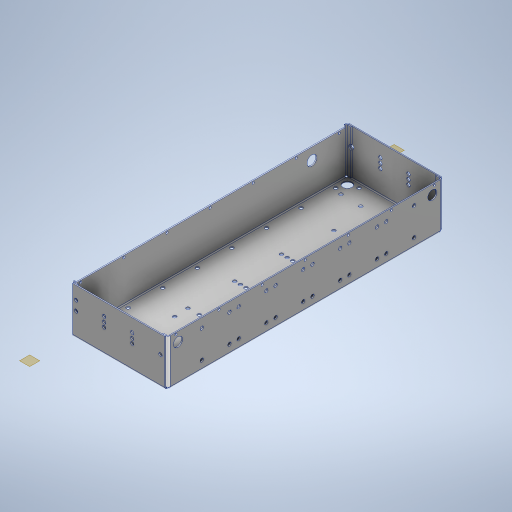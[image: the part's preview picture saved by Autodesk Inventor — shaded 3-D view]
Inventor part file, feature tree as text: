
AUTODESK INVENTOR PART (.ipt)
format: ipt  version: 2023 (Build 270158000, 158)  size: 754,176 bytes
history: native  units: in
note: dims shown in document units (in); Inventor stores cm internally (conversion verified against a paired STEP export)
features: sketch x25, hole x20, sheet_metal_op x12, pattern_linear x12, other x7, plane x4
ambient origin geometry x8: Origin, YZ Plane, XZ Plane, XY Plane, X Axis, Y Axis, Z Axis, Center Point
bodies: Solid1 (feature_tree)
feature tree (80):
  sheet_metal_op  "Face1"
  sheet_metal_op  "Flange1"
  sheet_metal_op  "Flange2"
  sheet_metal_op  "Unfold1"
  hole  "Hole1"  [1 undecoded]
  pattern_linear  "Rectangular Pattern1"  Count1=30  [1 undecoded]
  pattern_linear  "Rectangular Pattern2"  Count1=10  [1 undecoded]
  hole  "Hole2"  [1 undecoded]
  pattern_linear  "Rectangular Pattern3"  Count1=10 Spacing1=90.0deg
  hole  "Hole3"  [1 undecoded]
  hole  "Hole6"  [1 undecoded]
  pattern_linear  "Rectangular Pattern6"  Count1=10 Spacing1=90.0deg
  plane  "Work Plane4"
  hole  "Hole7"  [1 undecoded]
  plane  "Work Plane3"
  hole  "Hole8"  [1 undecoded]
  plane  "Work Plane2"
  hole  "Hole9"  [1 undecoded]
  plane  "Work Plane1"
  hole  "Hole10"  [1 undecoded]
  hole  "Hole11"  [1 undecoded]
  hole  "Hole12"  [1 undecoded]
  hole  "Hole13"  [1 undecoded]
  pattern_linear  "Rectangular Pattern11"  Count1=6  [1 undecoded]
  pattern_linear  "Rectangular Pattern12"  Count1=6  [1 undecoded]
  pattern_linear  "Rectangular Pattern13"  Count1=6  [1 undecoded]
  pattern_linear  "Rectangular Pattern14"  Count1=2  [1 undecoded]
  sheet_metal_op  "Refold6"
  sheet_metal_op  "Flange8"
  hole  "Hole14"  [1 undecoded]
  hole  "Hole15"  [1 undecoded]
  hole  "Hole16"  [1 undecoded]
  hole  "Hole17"  [1 undecoded]
  hole  "Hole18"  [1 undecoded]
  hole  "Hole19"  [1 undecoded]
  pattern_linear  "Rectangular Pattern15"  Count1=3  [1 undecoded]
  hole  "Hole20"  [1 undecoded]
  pattern_linear  "Rectangular Pattern16"  Count1=2  [1 undecoded]
  hole  "Hole21"  [1 undecoded]
  pattern_linear  "Rectangular Pattern17"  Count1=2  [1 undecoded]
  hole  "Hole22"  [1 undecoded]
  pattern_linear  "Rectangular Pattern18"  Spacing1=0.374in  [1 undecoded]
  sketch  "Sketch1"  dims[d0=23.622in d1=7.874in d2=11.811in d3=3.937in]
  other  "Plate1"
  sketch  "Sketch2"  dims[d4=0.0875in d5=0.0875in]
  other  "Plate2"
  sheet_metal_op  "Bend1"
  sheet_metal_op  "Corner1"
  sketch  "Sketch3"  dims[d6=0.0438in]
  other  "Plate3"
  sheet_metal_op  "Bend2"
  sheet_metal_op  "Corner2"
  sketch  "Sketch5"  dims[d7=0.175in]
  sketch  "Sketch6"  dims[d8=0.0875in d9=3.937in d10=90.0deg d11=0.0787in]
  sketch  "Sketch7"  dims[d12=0.35in d13=0.0875in]
  sketch  "Sketch10"  dims[d14=0.0875in d15=0.0875in]
  sketch  "Sketch11"  dims[d16=0.0438in]
  sketch  "Sketch13"  dims[d17=0.175in]
  sketch  "Sketch15"  dims[d18=0.0875in d19=3.937in d20=90.0deg d21=0.0787in]
  sketch  "Sketch16"  dims[d22=0.35in d23=0.0875in]
  sketch  "Sketch17"  dims[d24=0.0875in]
  sketch  "Sketch21"  dims[d35=0.2969in d36=0.2953in d37=0.1476in d38=0.0984in d39=90.0deg d40=0.0875in d41=0.8108in]
  sketch  "Sketch25"  dims[d42=0.7874in d44=0.9646in d46=1.1811in d48=3.9921in]
  sketch  "Sketch26"  dims[d49=0.2969in d50=0.2953in d51=0.1476in d52=0.0984in d53=90.0deg d54=0.3937in d55=0.8108in d56=0.9646in]
  other  "Plate9"
  sheet_metal_op  "Bend8"
  sheet_metal_op  "Corner8"
  sketch  "Sketch27"  dims[d57=0.9646in d58=0.4823in]
  sketch  "Sketch28"  dims[d59=1.1811in d61=3.9921in]
  sketch  "Sketch29"  dims[d62=0.7874in d63=0.2953in d64=0.1476in d65=0.0984in d66=90.0deg d67=0.3937in d68=0.8108in d69=0.5906in]
  sketch  "Sketch30"  dims[d70=0.5906in]
  sketch  "Sketch31"  dims[d95=0.2969in d96=0.2953in d97=0.1476in d98=0.0984in d99=90.0deg d100=0.0875in d101=0.8108in d102=2.3622in d103=2.3622in d104=2.3622in d105=0.7874in]
  sketch  "Sketch32"  dims[d106=2.3622in d107=2.3622in d109=3.1496in]
  sketch  "Sketch33"  dims[d110=0.2969in d111=0.2953in d112=0.1476in d113=0.0984in d114=90.0deg d115=0.0875in d116=0.8108in]
  sketch  "Sketch34"  dims[d122=0.2969in d123=0.2953in d124=0.1476in d125=0.0984in d126=90.0deg d127=0.3937in d128=0.8108in d129=0.8071in]
  sketch  "Sketch35"  dims[d130=0.4035in]
  sketch  "Sketch36"  dims[d134=0.2969in d135=0.2953in d136=0.1476in d137=0.0984in d138=90.0deg d139=0.3937in d140=0.8108in d144=0.2969in d145=0.2953in d146=0.1476in d147=0.0984in d148=90.0deg d149=0.3937in d150=0.8108in d151=0.8071in d158=0.2969in d159=0.2953in d160=0.1476in d161=0.0984in d162=90.0deg d163=0.3937in d164=0.8108in d165=1.9252in d166=2.6949in d167=1.1811in d168=0.9626in d169=0.7874in d170=0.2953in d171=0.1476in d172=0.0984in d173=90.0deg d174=0.3937in d175=0.8108in d176=0.7874in d177=0.2953in d178=0.1476in d179=0.0984in d180=90.0deg d181=0.3937in d182=0.8108in d183=0.7874in d184=0.7874in d185=0.7874in d186=0.7874in d188=0.374in d189=2.433in d190=0.3346in d191=2.433in d192=1.1811in d194=2.4016in d195=1.1811in d197=2.4016in d198=1.1811in d200=2.4016in d201=1.1811in d203=2.4016in d205=7.0866in d206=0.5316in d231=0.0984in d250=0.0591in d263=0.0197in d265=0.0197in d271=0.0875in d272=0.0in d273=0.0875in d274=0.0in d275=0.0875in d276=0.0438in d277=0.175in d278=0.0875in d279=0.4921in d280=90.0deg d281=0.0984in d282=0.35in d283=0.0875in d284=0.0875in d285=7.874in d286=2.4016in d287=0.4331in d288=0.2953in d289=0.1476in d290=0.0984in d291=90.0deg d292=0.0875in d293=0.0in d294=0.4331in d295=0.2953in d296=0.1476in d297=0.0984in d298=90.0deg d299=0.3937in d300=0.0in d301=0.8386in d302=0.2953in d303=0.1476in d304=0.0984in d305=90.0deg d306=0.0875in d307=0.8108in d308=0.2969in d309=0.2953in d310=0.1476in d311=0.0984in d312=90.0deg d313=0.3937in d314=0.8108in d316=2.2441in d319=0.2969in d320=0.2953in d321=0.1476in d322=0.0984in d323=90.0deg d324=0.3937in d325=0.8108in d326=1.0236in d327=1.5748in d328=2.9528in d329=2.5591in d330=1.0236in d331=2.7559in d332=0.5906in d333=0.0591in d334=0.2969in d335=0.2953in d336=0.1476in d337=0.0984in d338=90.0deg d339=0.0875in d340=0.8108in d341=0.5in d342=1.5in d343=3.1496in d345=2.9528in d346=0.7874in d348=7.2065in d349=0.2969in d350=0.2953in d351=0.1476in d352=0.0984in d353=90.0deg d354=0.0875in d355=0.8108in d356=0.5in d357=1.5in d358=1.1811in d360=2.9528in d361=0.7874in d363=22.622in d364=0.194in d365=0.2953in d366=0.1476in d367=0.0984in d368=90.0deg d369=0.0875in d370=0.8108in d371=0.5in d372=2.7559in d374=3.6755in d375=0.162in d376=0.2073in d377=0.0875in d378=0.0in d379=0.194in d380=0.2953in d381=0.1476in d382=0.0984in d383=90.0deg d384=0.0875in d385=0.8108in d386=0.5in d387=0.162in d388=2.7559in d390=3.6755in]
  other  "Cut4"
  other  "Cut5"
  other  "Cut6"
note: 30 required parameter values undecoded (feature->parameter linkage not recoverable at this tier; creation-order binding heuristic only, values carry confidence <= 0.55)
